annotation { "Feature Type Name" : "Feature", "Feature Type Description" : "" }
export const myFeature = defineFeature(function(context is Context, id is Id, definition is map)
    precondition{}
    {
        {
            var Q0;
            Q0=qCreatedBy(makeId("Top.planeOp"),FACE);
            var sketch = newSketch(context, id + "F0", { "sketchPlane" : qUnion([Q0])});
            skLineSegment(sketch, "E0", {"start": v(-165.1, 0) * mm, "end": v(165.1, 0) * mm});
            skLineSegment(sketch, "E1", {"start": v(-322.28, 203.2) * mm, "end": v(322.28, 203.2) * mm});
            skLineSegment(sketch, "E2", {"start": v(-322.28, 203.2) * mm, "end": v(-322.28, 0) * mm});
            skLineSegment(sketch, "E3", {"start": v(-322.28, 0) * mm, "end": v(-165.1, 0) * mm});
            skLineSegment(sketch, "E4", {"start": v(165.1, 0) * mm, "end": v(322.28, 0) * mm});
            skLineSegment(sketch, "E5", {"start": v(322.28, 203.2) * mm, "end": v(322.28, 0) * mm});
            skPoint(sketch, "E6", {"position": v(-165.1, -558.8) * mm});
            skLineSegment(sketch, "E7.bottom", {"start": v(-165.1, -558.8) * mm, "end": v(165.1, -558.8) * mm});
            skLineSegment(sketch, "E7.left", {"start": v(-165.1, -558.8) * mm, "end": v(-165.1, 0) * mm});
            skLineSegment(sketch, "E7.right", {"start": v(165.1, -558.8) * mm, "end": v(165.1, 0) * mm});
            skSolve(sketch);
        }
        {
            var Q0;
            Q0=makeQuery(id+"F0.imprint","IMPRINT",FACE,{"disambiguationData":[TD([[makeQuery(id+"F0.imprint","IMPRINT",EDGE,{"derivedFrom":sQuery(id+"F0.wireOp",EDGE,"E1")}),-1.0]])]});
            var Q1;
            Q1=makeQuery(id+"F0.imprint","IMPRINT",FACE,{"disambiguationData":[TD([[makeQuery(id+"F0.imprint","IMPRINT",EDGE,{"derivedFrom":sQuery(id+"F0.wireOp",EDGE,"E7.bottom")}),1.0]])]});
            extrude(context, id + "F1", {"entities" : qUnion([Q0, Q1]), "depth" : 76.2 * mm, "offsetDistance" : 25.4 * mm});
        }
        {
            var Q0;
            Q0=makeQuery(id+"F1.opExtrude","CAP_FACE",FACE,{"disambiguationData":[OSD([sQuery(id+"F0.wireOp",EDGE,"E1"),sQuery(id+"F0.wireOp",EDGE,"E2"),sQuery(id+"F0.wireOp",EDGE,"E3"),sQuery(id+"F0.wireOp",EDGE,"E4"),sQuery(id+"F0.wireOp",EDGE,"E5"),sQuery(id+"F0.wireOp",EDGE,"E7.bottom"),sQuery(id+"F0.wireOp",EDGE,"E7.left"),sQuery(id+"F0.wireOp",EDGE,"E7.right")])],"isStart":false});
            var sketch = newSketch(context, id + "F2", { "sketchPlane" : qUnion([Q0])});
            skText(sketch, "E8", { "text": "Electronics Compartment", "fontName": "AllertaStencil-Regular.ttf"});
            const initialGuessF2  = {"E8": [0.00354, -0.47534, 0, 1, 0.03148]};
            skSetInitialGuess(sketch, initialGuessF2);
            skSolve(sketch);
        }
        {
            var Q0;
            Q0 = qSketchRegion(id + "F2", true);
            extrude(context, id + "F3", {"entities" : qUnion([Q0]), "operationType" : NewBodyOperationType.REMOVE, "oppositeDirection" : true, "depth" : 6.35 * mm, "offsetDistance" : 25.4 * mm});
        }
    });